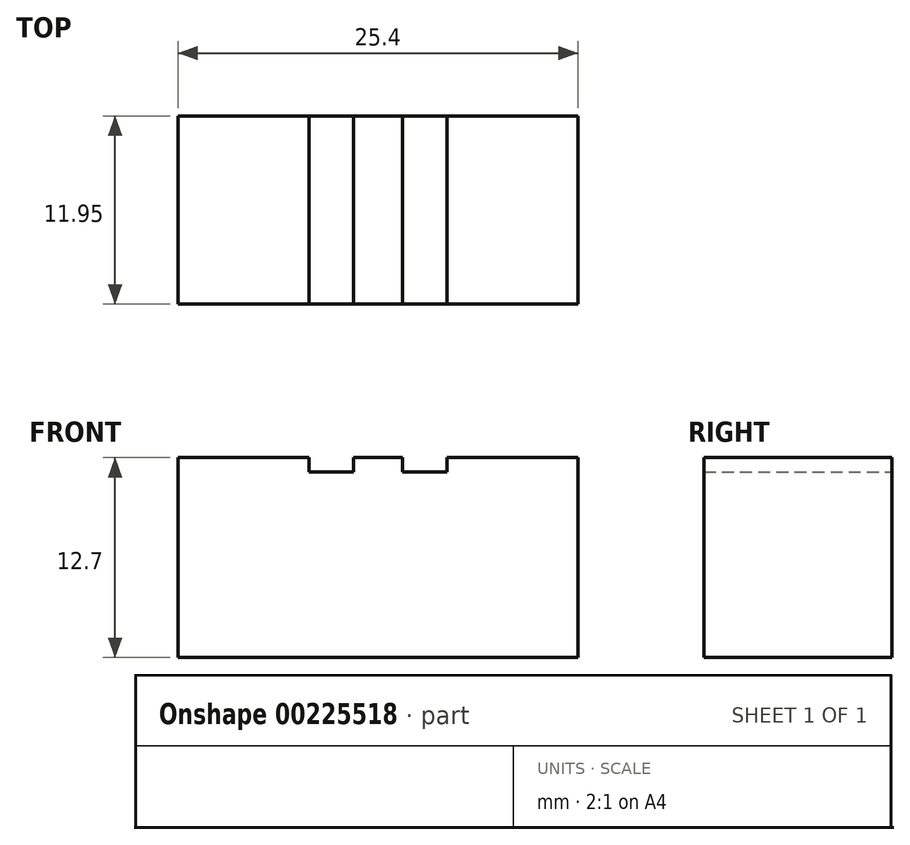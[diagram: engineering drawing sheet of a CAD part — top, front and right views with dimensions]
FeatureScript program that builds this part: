
annotation { "Feature Type Name" : "Feature", "Feature Type Description" : "" }
export const myFeature = defineFeature(function(context is Context, id is Id, definition is map)
    precondition{}
    {
        {
            var Q0;
            Q0=qCreatedBy(makeId("Front.planeOp"),FACE);
            var sketch = newSketch(context, id + "F0", { "sketchPlane" : qUnion([Q0])});
            skLineSegment(sketch, "E0", {"start": v(-12.7, 12.7) * mm, "end": v(-12.7, 0) * mm});
            skLineSegment(sketch, "E1", {"start": v(-12.7, 0) * mm, "end": v(12.7, 0) * mm});
            skLineSegment(sketch, "E2", {"start": v(12.7, 0) * mm, "end": v(12.7, 12.7) * mm});
            skLineSegment(sketch, "E3", {"start": v(12.7, 12.7) * mm, "end": v(4.38, 12.7) * mm});
            skLineSegment(sketch, "E4", {"start": v(4.38, 12.7) * mm, "end": v(4.38, 11.78) * mm});
            skLineSegment(sketch, "E5", {"start": v(4.38, 11.78) * mm, "end": v(1.56, 11.78) * mm});
            skLineSegment(sketch, "E6", {"start": v(1.56, 11.78) * mm, "end": v(1.56, 12.7) * mm});
            skLineSegment(sketch, "E7", {"start": v(1.56, 12.7) * mm, "end": v(-1.56, 12.7) * mm});
            skLineSegment(sketch, "E8", {"start": v(-1.56, 12.7) * mm, "end": v(-1.56, 11.78) * mm});
            skLineSegment(sketch, "E9", {"start": v(-1.56, 11.78) * mm, "end": v(-4.38, 11.78) * mm});
            skLineSegment(sketch, "E10", {"start": v(-4.38, 11.78) * mm, "end": v(-4.38, 12.7) * mm});
            skLineSegment(sketch, "E11", {"start": v(-4.38, 12.7) * mm, "end": v(-12.7, 12.7) * mm});
            skLineSegment(sketch, "E12.0", {"start": v(0.62, 11.78) * mm, "end": v(0.62, 12.7) * mm});
            skSolve(sketch);
        }
        {
            var Q0;
            Q0=makeQuery(id+"F0.imprint","IMPRINT",FACE,{"disambiguationData":[TD([[makeQuery(id+"F0.imprint","IMPRINT",EDGE,{"derivedFrom":sQuery(id+"F0.wireOp",EDGE,"E0")}),1.0]])]});
            extrude(context, id + "F1", {"entities" : qUnion([Q0]), "depth" : 11.95 * mm});
        }
    });
